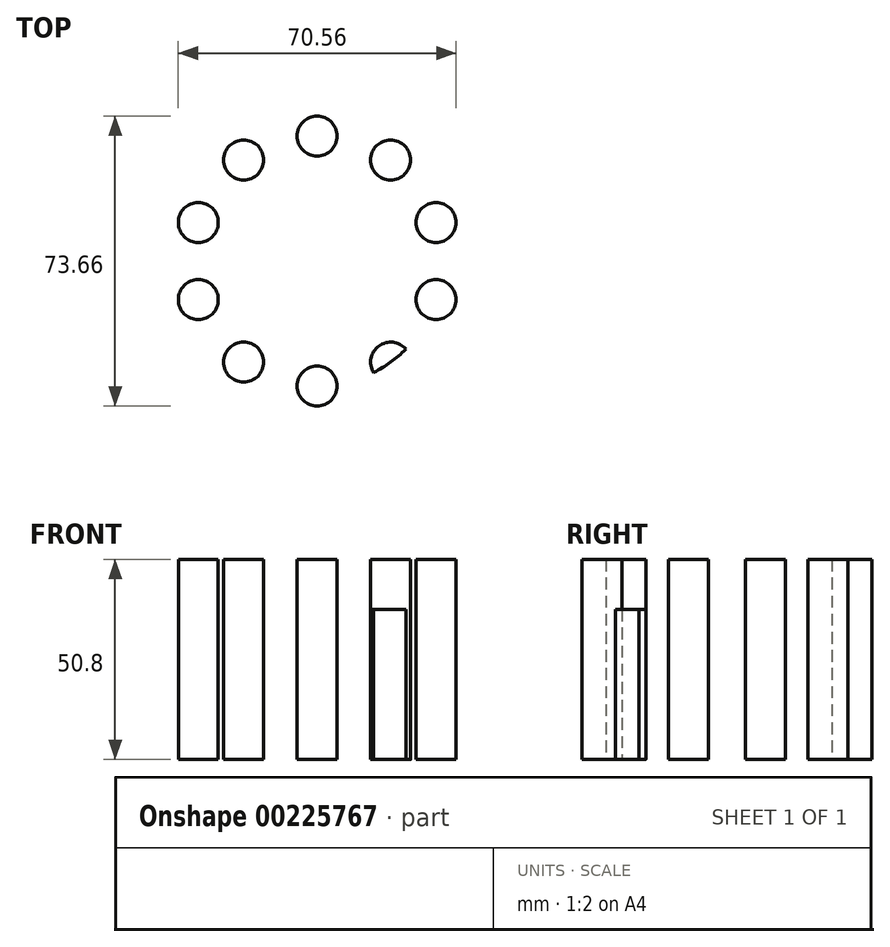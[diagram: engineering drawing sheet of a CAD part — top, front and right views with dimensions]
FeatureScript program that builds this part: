
annotation { "Feature Type Name" : "Feature", "Feature Type Description" : "" }
export const myFeature = defineFeature(function(context is Context, id is Id, definition is map)
    precondition{}
    {
        {
            var Q0;
            Q0=qCreatedBy(makeId("Top.planeOp"),FACE);
            var sketch = newSketch(context, id + "F0", { "sketchPlane" : qUnion([Q0])});
            skCircle(sketch, "E0", {"center": v(0, 0) * mm, "radius": 31.75 * mm});
            skSolve(sketch);
        }
        {
            var Q0;
            Q0=qSketchRegion(id+"F0",true);
            extrude(context, id + "F1", {"entities" : qUnion([Q0]), "depth" : 38.1 * mm});
        }
        {
            var Q0;
            Q0=qCreatedBy(makeId("Top.planeOp"),FACE);
            var sketch = newSketch(context, id + "F2", { "sketchPlane" : qUnion([Q0])});
            skCircle(sketch, "E1", {"center": v(0, 31.75) * mm, "radius": 5.08 * mm});
            skCircle(sketch, "E2.1.0", {"center": v(-18.66, 25.69) * mm, "radius": 5.08 * mm});
            skCircle(sketch, "E2.2.0", {"center": v(-30.2, 9.81) * mm, "radius": 5.08 * mm});
            skCircle(sketch, "E2.3.0", {"center": v(-30.2, -9.81) * mm, "radius": 5.08 * mm});
            skCircle(sketch, "E2.4.0", {"center": v(-18.66, -25.69) * mm, "radius": 5.08 * mm});
            skCircle(sketch, "E2.5.0", {"center": v(0, -31.75) * mm, "radius": 5.08 * mm});
            skCircle(sketch, "E2.6.0", {"center": v(18.66, -25.69) * mm, "radius": 5.08 * mm});
            skCircle(sketch, "E2.7.0", {"center": v(30.2, -9.81) * mm, "radius": 5.08 * mm});
            skCircle(sketch, "E2.8.0", {"center": v(30.2, 9.81) * mm, "radius": 5.08 * mm});
            skCircle(sketch, "E2.9.0", {"center": v(18.66, 25.69) * mm, "radius": 5.08 * mm});
            skPoint(sketch, "E2.center", {"position": v(0, 0) * mm});
            skSolve(sketch);
        }
        {
            var Q0;
            Q0=qSketchRegion(id+"F2",true);
            extrude(context, id + "F3", {"entities" : qUnion([Q0]), "depth" : 50.8 * mm});
        }
        {
            var Q0;
            Q0=makeQuery(id+"F1.opExtrude","SWEPT_BODY",BODY,{"disambiguationData":[OSD([sQuery(id+"F0.wireOp",EDGE,"E0")])]});
            var Q1;
            Q1=makeQuery(id+"F3.opExtrude","SWEPT_BODY",BODY,{"disambiguationData":[OSD([sQuery(id+"F2.wireOp",EDGE,"E2.6.0")])]});
            booleanBodies(context, id + "F4", {"operationType" : BooleanOperationType.INTERSECTION, "tools" : qUnion([Q0, Q1])});
        }
    });
